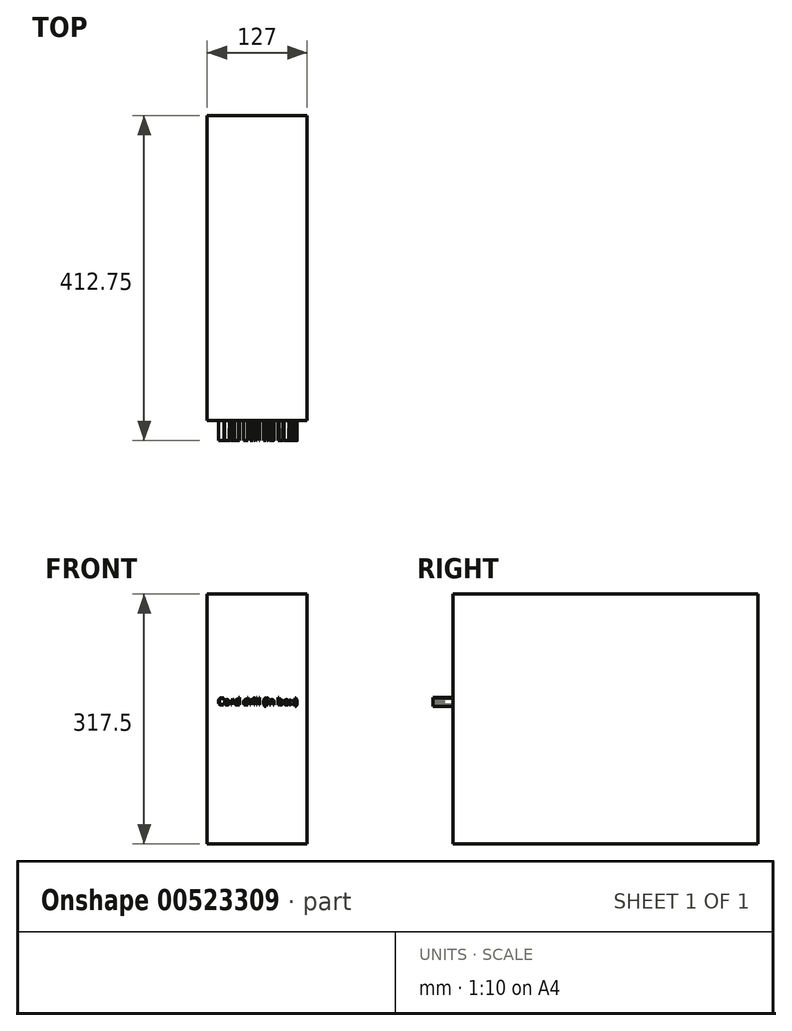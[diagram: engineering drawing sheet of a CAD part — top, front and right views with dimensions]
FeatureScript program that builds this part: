
annotation { "Feature Type Name" : "Feature", "Feature Type Description" : "" }
export const myFeature = defineFeature(function(context is Context, id is Id, definition is map)
    precondition{}
    {
        {
            var Q0;
            Q0=qCreatedBy(makeId("Front.planeOp"),FACE);
            var sketch = newSketch(context, id + "F0", { "sketchPlane" : qUnion([Q0])});
            skLineSegment(sketch, "E0.bottom", {"start": v(63.5, 158.75) * mm, "end": v(-63.5, 158.75) * mm});
            skLineSegment(sketch, "E0.top", {"start": v(63.5, -158.75) * mm, "end": v(-63.5, -158.75) * mm});
            skLineSegment(sketch, "E0.left", {"start": v(63.5, 158.75) * mm, "end": v(63.5, -158.75) * mm});
            skLineSegment(sketch, "E0.right", {"start": v(-63.5, 158.75) * mm, "end": v(-63.5, -158.75) * mm});
            skPoint(sketch, "E0.middle", {"position": v(0, 0) * mm});
            skSolve(sketch);
        }
        {
            var Q0;
            Q0=makeQuery(id+"F0.imprint","IMPRINT",FACE,{"disambiguationData":[TD([[makeQuery(id+"F0.imprint","IMPRINT",EDGE,{"derivedFrom":sQuery(id+"F0.wireOp",EDGE,"E0.bottom")}),1.0]])]});
            extrude(context, id + "F1", {"entities" : qUnion([Q0]), "depth" : 387.35 * mm, "offsetDistance" : 25.4 * mm});
        }
        {
            var Q0;
            Q0=makeQuery(id+"F1.opExtrude","CAP_FACE",FACE,{"disambiguationData":[OSD([sQuery(id+"F0.wireOp",EDGE,"E0.bottom"),sQuery(id+"F0.wireOp",EDGE,"E0.top"),sQuery(id+"F0.wireOp",EDGE,"E0.left"),sQuery(id+"F0.wireOp",EDGE,"E0.right")])],"isStart":false});
            var sketch = newSketch(context, id + "F2", { "sketchPlane" : qUnion([Q0])});
            skText(sketch, "E1", { "text": "Cord drill (in box)", "fontName": "OpenSans-Regular.ttf"});
            const initialGuessF2  = {"E1": [-0.05007, 0.01769, 1, 0, 0.0091]};
            skSetInitialGuess(sketch, initialGuessF2);
            skSolve(sketch);
        }
        {
            var Q0;
            Q0 = qSketchRegion(id + "F2", true);
            extrude(context, id + "F3", {"entities" : qUnion([Q0]), "operationType" : NewBodyOperationType.ADD, "depth" : 25.4 * mm, "offsetDistance" : 25.4 * mm});
        }
    });
